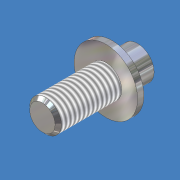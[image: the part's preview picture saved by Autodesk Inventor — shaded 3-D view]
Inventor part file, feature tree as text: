
AUTODESK INVENTOR PART (.ipt)
format: ipt  version: unknown  size: 184,320 bytes
history: native  units: mm (DEFAULTED — no unit token found)
features: extrude x3, sketch x3, chamfer x1, thread x1
ambient origin geometry x8: Origin, YZ Plane, XZ Plane, XY Plane, X Axis, Y Axis, Z Axis, Center Point
bodies: Solid1 (feature_tree)
feature tree (8):
  extrude  "Extrusion1"  Depth=1.27mm TaperAngle=0.0deg
  extrude  "Extrusion2"  Depth=12.7mm TaperAngle=0.0deg
  chamfer  "Chamfer1"  Distance=0.635mm
  thread  "Thread1"  [1 undecoded]
  extrude  "Extrusion3"  Depth=5.08mm TaperAngle=0.0deg
  sketch  "Sketch1"  dims[d0=12.7mm d1=1.27mm d2=0.0mm]
  sketch  "Sketch2"  dims[d3=6.35mm d4=12.7mm d5=0.0mm d6=0.635mm d7=0.635mm d8=25.4mm d9=0.0mm]
  sketch  "Sketch3"  dims[d10=6.604mm d11=5.08mm d12=0.0mm d13=45.0deg]
note: 1 required parameter value undecoded (feature->parameter linkage not recoverable at this tier; creation-order binding heuristic only, values carry confidence <= 0.55)
